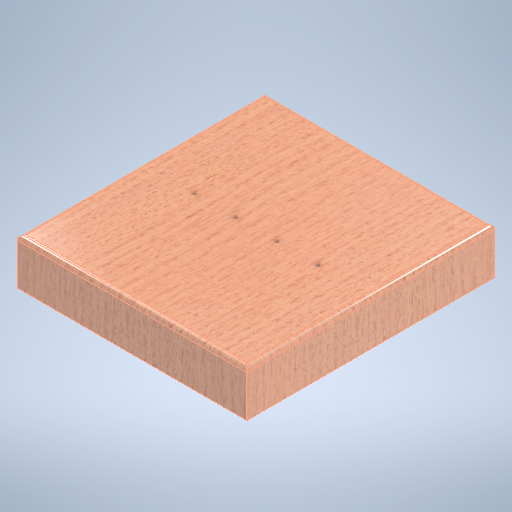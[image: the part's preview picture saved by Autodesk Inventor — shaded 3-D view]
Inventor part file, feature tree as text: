
AUTODESK INVENTOR PART (.ipt)
format: ipt  version: 2025.1 (Build 291241000, 241)  size: 415,744 bytes
history: native  units: mm
features: sketch x2, extrude x1, fillet x1, hole x1
ambient origin geometry x8: Origin, YZ Plane, XZ Plane, XY Plane, X Axis, Y Axis, Z Axis, Center Point
bodies: Solid1 (feature_tree)
feature tree (5):
  extrude  "Extrusion1"  Depth=250.0mm
  fillet  "Fillet1"  Radius=50.0mm
  hole  "Hole1"  [1 undecoded]
  sketch  "Sketch1"  dims[d0=270.0mm d1=250.0mm d2=50.0mm d3=0.0mm]
  sketch  "Sketch2"  dims[d4=5.0mm d5=135.0mm d6=45.0mm d7=45.0mm d8=45.0mm d10=67.5mm d11=5.0mm d12=6.0mm d13=4.0mm d14=2.0mm d15=90.0deg d16=8.0mm d17=0.0mm]
note: 1 required parameter value undecoded (feature->parameter linkage not recoverable at this tier; creation-order binding heuristic only, values carry confidence <= 0.55)
